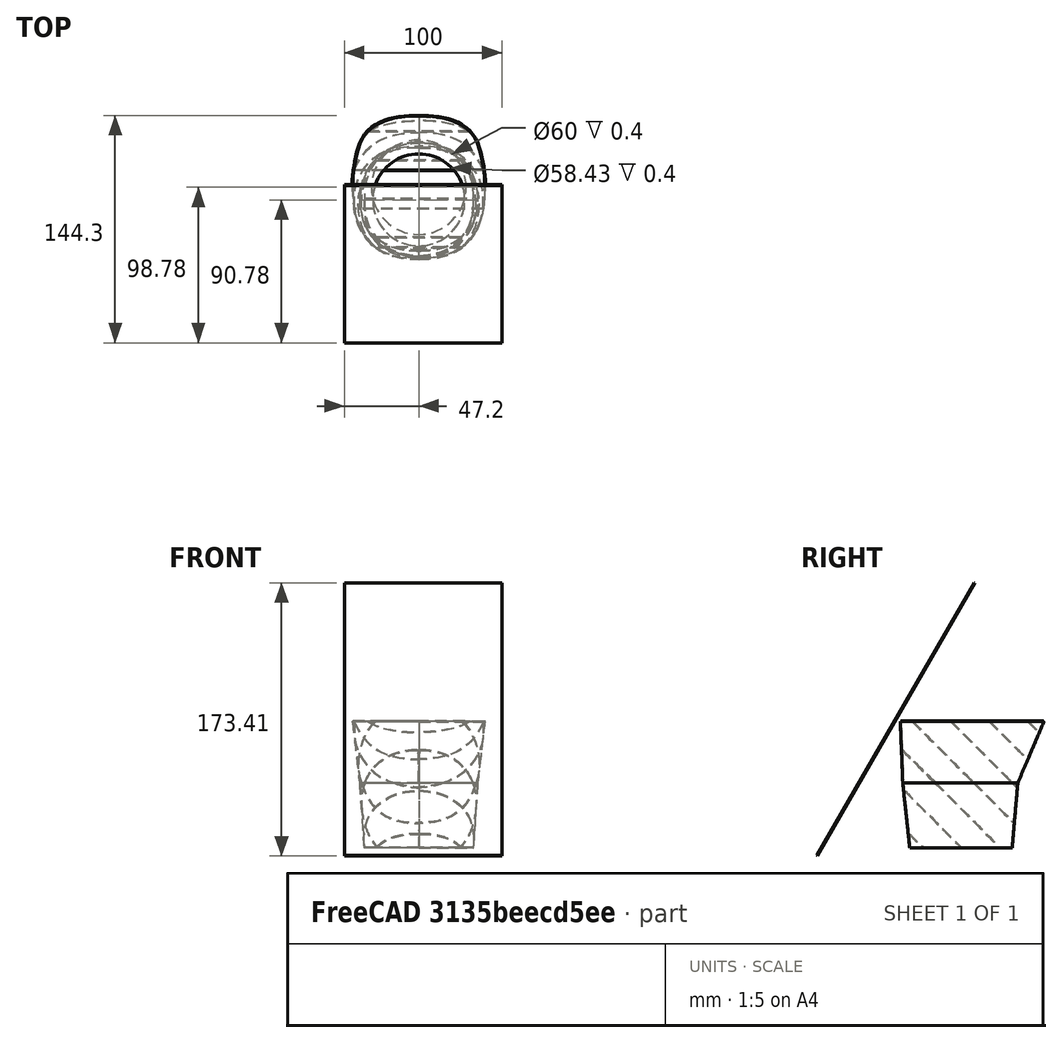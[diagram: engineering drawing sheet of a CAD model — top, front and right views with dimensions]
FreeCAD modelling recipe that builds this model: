
FCSTD DOCUMENT  (FreeCAD 0.21R33694 (Git))
Label: nose
License: All rights reserved
LicenseURL: http://en.wikipedia.org/wiki/All_rights_reserved
objects: Sketcher::SketchObject×14, PartDesign::Body×7, PartDesign::AdditiveLoft×6, Image::ImagePlane×4, Part::MultiFuse×3, PartDesign::Thickness×2, Part::Box×2, Part::MultiCommon×2, App::MeasureDistance×1, Part::FeaturePython×1, Part::Cylinder×1, Part::Cut×1, PartDesign::Pad×1, PartDesign::Pocket×1
note: 50 computed .brp shape members not serialized (recipe doc carries the construction recipe); baked Part::Feature solids carry a one-line shape summary decoded from their .brp

FEATURE [Image::ImagePlane] Screenshot_from_2023_10_14_23_56_05  label="Screenshot from 2023-10-14 23-56-05"
  Placement = pos=(-1.3,0,0) rot=(0,0,1;0rad)
  XSize = 117.558
  YSize = 96.0835
FEATURE [Image::ImagePlane] Screenshot_from_2023_10_14_23_55_51  label="Screenshot from 2023-10-14 23-55-51"
  Placement = pos=(-6,0.8,0) rot=(0,0,1;0rad)
  XSize = 153.658
  YSize = 119.36
FEATURE [Image::ImagePlane] Screenshot_from_2023_10_14_23_56_29  label="Screenshot from 2023-10-14 23-56-29"
  Placement = pos=(-8.1,5.1,0) rot=(0,0,1;0rad)
  XSize = 174.967
  YSize = 118.829
FEATURE [Sketcher::SketchObject] Sketch
  FullyConstrained = false
  MapMode = 5
  Support = -> [XY_Plane]
  sketch-geometry (10):
    g0-g4: Circle x5 (B-spline internal-alignment scaffolding for g5; pole/knot coordinates omitted)
    g5: BSplineCurve PolesCount=5 KnotsCount=3 Degree=3 IsPeriodic=0
    g6: GeomPoint X=0 Y=32.9051 Z=0
    g7: GeomPoint X=34.5313 Y=0.497786 Z=0
    g8: GeomPoint X=0 Y=-31.3846 Z=0
    g9: BSplineCurve PolesCount=5 KnotsCount=3 Degree=3 IsPeriodic=0
  constraints (12):
    c: Weight(g0) = 1
    c: PointOnObject(g5,g-2)
    c: Equal(g0,g1)
    c: Equal(g0,g2)
    c: PointOnObject(g2,g-1)
    c: Equal(g0,g3)
    c: Equal(g0,g4)
    c: PointOnObject(g5,g-2)
    c: InternalAlignment(g0-g4 -> g5) x5
    c: InternalAlignment(g6,g5)
    c: InternalAlignment(g7,g5)
    c: InternalAlignment(g8,g5)
FEATURE [Sketcher::SketchObject] Sketch001
  AttachmentOffset = pos=(0,0,41) rot=(0,0,1;0rad)
  FullyConstrained = false
  MapMode = 5
  Placement = pos=(0,0,41) rot=(0,0,1;0rad)
  Support = -> [XY_Plane]
  sketch-geometry (10):
    g0-g4: Circle x5 (B-spline internal-alignment scaffolding for g5; pole/knot coordinates omitted)
    g5: BSplineCurve PolesCount=5 KnotsCount=3 Degree=3 IsPeriodic=0
    g6: GeomPoint X=0 Y=36.497 Z=0
    g7: GeomPoint X=37.3042 Y=0.119484 Z=0
    g8: GeomPoint X=0 Y=-35.8137 Z=0
    g9: BSplineCurve PolesCount=5 KnotsCount=3 Degree=3 IsPeriodic=0
  constraints (12):
    c: Weight(g0) = 1
    c: PointOnObject(g5,g-2)
    c: Equal(g0,g1)
    c: Equal(g0,g2)
    c: PointOnObject(g2,g-1)
    c: Equal(g0,g3)
    c: Equal(g0,g4)
    c: PointOnObject(g5,g-2)
    c: InternalAlignment(g0-g4 -> g5) x5
    c: InternalAlignment(g6,g5)
    c: InternalAlignment(g7,g5)
    c: InternalAlignment(g8,g5)
FEATURE [Sketcher::SketchObject] Sketch004
  AttachmentOffset = pos=(0,0,41) rot=(0,0,1;0rad)
  FullyConstrained = false
  MapMode = 5
  Placement = pos=(0,0,41) rot=(0,0,1;0rad)
  Support = -> [XY_Plane001]
  sketch-geometry (10):
    g0-g4: Circle x5 (B-spline internal-alignment scaffolding for g5; pole/knot coordinates omitted)
    g5: BSplineCurve PolesCount=5 KnotsCount=3 Degree=3 IsPeriodic=0
    g6: GeomPoint X=0 Y=36.497 Z=0
    g7: GeomPoint X=37.3042 Y=0.119484 Z=0
    g8: GeomPoint X=0 Y=-35.8137 Z=0
    g9: BSplineCurve PolesCount=5 KnotsCount=3 Degree=3 IsPeriodic=0
  constraints (12):
    c: Weight(g0) = 1
    c: PointOnObject(g5,g-2)
    c: Equal(g0,g1)
    c: Equal(g0,g2)
    c: PointOnObject(g2,g-1)
    c: Equal(g0,g3)
    c: Equal(g0,g4)
    c: PointOnObject(g5,g-2)
    c: InternalAlignment(g0-g4 -> g5) x5
    c: InternalAlignment(g6,g5)
    c: InternalAlignment(g7,g5)
    c: InternalAlignment(g8,g5)
FEATURE [Sketcher::SketchObject] Sketch005
  AttachmentOffset = pos=(0,0,80) rot=(0,0,1;0rad)
  FullyConstrained = false
  MapMode = 5
  Placement = pos=(0,0,80) rot=(0,0,1;0rad)
  Support = -> [XY_Plane001]
  sketch-geometry (16):
    g0-g7: Circle x8 (B-spline internal-alignment scaffolding for g8; pole/knot coordinates omitted)
    g8: BSplineCurve PolesCount=8 KnotsCount=6 Degree=3 IsPeriodic=0
    g9-g14: GeomPoint x6 (B-spline internal-alignment scaffolding for g8; pole/knot coordinates omitted)
    g15: BSplineCurve PolesCount=8 KnotsCount=6 Degree=3 IsPeriodic=0
  constraints (10):
    c: Weight(g0) = 1
    c: PointOnObject(g8,g-2)
    c: Equal(g0, g1-g4) x4
    c: PointOnObject(g4,g-1)
    c: Equal(g0,g5)
    c: Equal(g0,g6)
    c: Equal(g0,g7)
    c: PointOnObject(g8,g-2)
    c: InternalAlignment(g0-g7 -> g8) x8
    c: InternalAlignment(g9-g14 -> g8) x6
FEATURE [PartDesign::AdditiveLoft] AdditiveLoft
  Closed = false
  Profile = -> Sketch001
  Ruled = true
  Sections = -> [Sketch]
FEATURE [PartDesign::AdditiveLoft] AdditiveLoft001
  Closed = false
  Profile = -> Sketch005
  Ruled = true
  Sections = -> [Sketch004]
FEATURE [App::MeasureDistance] Distance  label="Distance: 64.29 mm"
  Distance = 64.2866
  P1 = (-0.105968,32.9036,0)
  P2 = (-0.0834491,-31.3831,0)
FEATURE [Image::ImagePlane] Screenshot_from_2023_10_15_16_07_44  label="Screenshot from 2023-10-15 16-07-44"
  Placement = pos=(-1e-14,17.7,44.9) rot=(0,1,0;4.71239rad)
  XSize = 263.435
  YSize = 168.665
FEATURE [Sketcher::SketchObject] Sketch006
  AttachmentOffset = pos=(0,0,41) rot=(0,0,1;0rad)
  FullyConstrained = false
  MapMode = 5
  Placement = pos=(0,0,41) rot=(0,0,1;0rad)
  Support = -> [XY_Plane002]
  sketch-geometry (10):
    g0-g4: Circle x5 (B-spline internal-alignment scaffolding for g5; pole/knot coordinates omitted)
    g5: BSplineCurve PolesCount=5 KnotsCount=3 Degree=3 IsPeriodic=0
    g6: GeomPoint X=0 Y=36.497 Z=0
    g7: GeomPoint X=37.3042 Y=0.119484 Z=0
    g8: GeomPoint X=0 Y=-35.8137 Z=0
    g9: BSplineCurve PolesCount=5 KnotsCount=3 Degree=3 IsPeriodic=0
  constraints (12):
    c: Weight(g0) = 1
    c: PointOnObject(g5,g-2)
    c: Equal(g0,g1)
    c: Equal(g0,g2)
    c: PointOnObject(g2,g-1)
    c: Equal(g0,g3)
    c: Equal(g0,g4)
    c: PointOnObject(g5,g-2)
    c: InternalAlignment(g0-g4 -> g5) x5
    c: InternalAlignment(g6,g5)
    c: InternalAlignment(g7,g5)
    c: InternalAlignment(g8,g5)
FEATURE [Sketcher::SketchObject] Sketch007
  AttachmentOffset = pos=(0,0,80) rot=(0,0,1;0rad)
  FullyConstrained = false
  MapMode = 5
  Placement = pos=(0,0,80) rot=(0,0,1;0rad)
  Support = -> [XY_Plane002]
  sketch-geometry (16):
    g0-g7: Circle x8 (B-spline internal-alignment scaffolding for g8; pole/knot coordinates omitted)
    g8: BSplineCurve PolesCount=8 KnotsCount=6 Degree=3 IsPeriodic=0
    g9-g14: GeomPoint x6 (B-spline internal-alignment scaffolding for g8; pole/knot coordinates omitted)
    g15: BSplineCurve PolesCount=8 KnotsCount=6 Degree=3 IsPeriodic=0
  constraints (10):
    c: Weight(g0) = 1
    c: PointOnObject(g8,g-2)
    c: Equal(g0, g1-g4) x4
    c: PointOnObject(g4,g-1)
    c: Equal(g0,g5)
    c: Equal(g0,g6)
    c: Equal(g0,g7)
    c: PointOnObject(g8,g-2)
    c: InternalAlignment(g0-g7 -> g8) x8
    c: InternalAlignment(g9-g14 -> g8) x6
FEATURE [PartDesign::AdditiveLoft] AdditiveLoft002
  Closed = false
  Profile = -> Sketch007
  Ruled = true
  Sections = -> [Sketch006]
FEATURE [PartDesign::Body] Body002
  Group = -> [Sketch006,Sketch007,AdditiveLoft002]
  Origin = -> Origin002
  Tip = -> AdditiveLoft002
FEATURE [Sketcher::SketchObject] Sketch008
  FullyConstrained = false
  MapMode = 5
  Support = -> [XY_Plane003]
  sketch-geometry (10):
    g0-g4: Circle x5 (B-spline internal-alignment scaffolding for g5; pole/knot coordinates omitted)
    g5: BSplineCurve PolesCount=5 KnotsCount=3 Degree=3 IsPeriodic=0
    g6: GeomPoint X=0 Y=32.9051 Z=0
    g7: GeomPoint X=34.5313 Y=0.497786 Z=0
    g8: GeomPoint X=0 Y=-31.3846 Z=0
    g9: BSplineCurve PolesCount=5 KnotsCount=3 Degree=3 IsPeriodic=0
  constraints (12):
    c: Weight(g0) = 1
    c: PointOnObject(g5,g-2)
    c: Equal(g0,g1)
    c: Equal(g0,g2)
    c: PointOnObject(g2,g-1)
    c: Equal(g0,g3)
    c: Equal(g0,g4)
    c: PointOnObject(g5,g-2)
    c: InternalAlignment(g0-g4 -> g5) x5
    c: InternalAlignment(g6,g5)
    c: InternalAlignment(g7,g5)
    c: InternalAlignment(g8,g5)
FEATURE [Sketcher::SketchObject] Sketch009
  AttachmentOffset = pos=(0,0,41) rot=(0,0,1;0rad)
  FullyConstrained = false
  MapMode = 5
  Placement = pos=(0,0,41) rot=(0,0,1;0rad)
  Support = -> [XY_Plane003]
  sketch-geometry (10):
    g0-g4: Circle x5 (B-spline internal-alignment scaffolding for g5; pole/knot coordinates omitted)
    g5: BSplineCurve PolesCount=5 KnotsCount=3 Degree=3 IsPeriodic=0
    g6: GeomPoint X=0 Y=36.497 Z=0
    g7: GeomPoint X=37.3042 Y=0.119484 Z=0
    g8: GeomPoint X=0 Y=-35.8137 Z=0
    g9: BSplineCurve PolesCount=5 KnotsCount=3 Degree=3 IsPeriodic=0
  constraints (12):
    c: Weight(g0) = 1
    c: PointOnObject(g5,g-2)
    c: Equal(g0,g1)
    c: Equal(g0,g2)
    c: PointOnObject(g2,g-1)
    c: Equal(g0,g3)
    c: Equal(g0,g4)
    c: PointOnObject(g5,g-2)
    c: InternalAlignment(g0-g4 -> g5) x5
    c: InternalAlignment(g6,g5)
    c: InternalAlignment(g7,g5)
    c: InternalAlignment(g8,g5)
FEATURE [PartDesign::AdditiveLoft] AdditiveLoft003
  Closed = false
  Profile = -> Sketch009
  Ruled = true
  Sections = -> [Sketch008]
FEATURE [PartDesign::Body] Body003
  Group = -> [Sketch008,Sketch009,AdditiveLoft003]
  Origin = -> Origin003
  Tip = -> AdditiveLoft003
FEATURE [PartDesign::Thickness] Thickness
  Base = -> AdditiveLoft [Face1]
  BaseFeature = -> AdditiveLoft
  Intersection = false
  Join = 1
  Mode = 0
  SupportTransform = false
  Value = 0.4
FEATURE [PartDesign::Body] Body
  Group = -> [Sketch,Sketch001,AdditiveLoft,Thickness]
  Origin = -> Origin
  Tip = -> Thickness
FEATURE [PartDesign::Thickness] Thickness001
  Base = -> AdditiveLoft001 [Face1,Face3]
  BaseFeature = -> AdditiveLoft001
  Intersection = false
  Join = 1
  Mode = 1
  SupportTransform = false
  Value = 0.4
FEATURE [PartDesign::Body] Body001
  Group = -> [Sketch004,Sketch005,AdditiveLoft001,Thickness001]
  Origin = -> Origin001
  Tip = -> Thickness001
FEATURE [Part::MultiFuse] Fusion001
  Shapes = -> [Body002,Body003]
FEATURE [Part::Box] Box  label="Cube"
  AttacherType = Attacher::AttachEngine3D
  Height = 200
  Length = 100
  Placement = pos=(-47.2,-90.7758,-5.26929) rot=(-1,0,0;0.523599rad)
  Width = 0.4
FEATURE [Part::FeaturePython] Array  # Draft array (typed FeaturePython)
  AlwaysSyncPlacement = false
  Angle = 360
  ArrayType = 0
  Axis = (0,0,1)
  Base = -> Box
  Center = (0,0,0)
  Count = 9
  ExpandArray = false
  Fuse = false
  IntervalAxis = (0,0,0)
  IntervalX = (100,0,0)
  IntervalY = (0,20,0)
  IntervalZ = (0,0,20)
  NumberCircles = 3
  NumberPolar = 5
  NumberX = 1
  NumberY = 9
  NumberZ = 1
  Placement = pos=(0,84.5954,-1.10956) rot=(1,0,0;1.309rad)
  PlacementList = 9 placements: arithmetic series from (-47.2,-90.7758,-5.26929) step (0,20,0) to (-47.2,69.2242,-5.26929)
  RadialDistance = 50
  ScaleList = (9) [(1,1,1),(1,1,1),(1,1,1),(1,1,1),(1,1,1),(1,1,1),(1,1,1),(1,1,1),(1,1,1)]
  Symmetry = 1
  TangentialDistance = 25
FEATURE [Part::MultiCommon] Common
  Shapes = -> [Fusion001,Array]
FEATURE [Sketcher::SketchObject] Sketch010
  AttachmentOffset = pos=(0,0,41) rot=(0,0,1;0rad)
  FullyConstrained = false
  MapMode = 5
  Placement = pos=(0,0,41) rot=(0,0,1;0rad)
  Support = -> [XY_Plane004]
  sketch-geometry (10):
    g0-g4: Circle x5 (B-spline internal-alignment scaffolding for g5; pole/knot coordinates omitted)
    g5: BSplineCurve PolesCount=5 KnotsCount=3 Degree=3 IsPeriodic=0
    g6: GeomPoint X=0 Y=36.497 Z=0
    g7: GeomPoint X=37.3042 Y=0.119484 Z=0
    g8: GeomPoint X=0 Y=-35.8137 Z=0
    g9: BSplineCurve PolesCount=5 KnotsCount=3 Degree=3 IsPeriodic=0
  constraints (12):
    c: Weight(g0) = 1
    c: PointOnObject(g5,g-2)
    c: Equal(g0,g1)
    c: Equal(g0,g2)
    c: PointOnObject(g2,g-1)
    c: Equal(g0,g3)
    c: Equal(g0,g4)
    c: PointOnObject(g5,g-2)
    c: InternalAlignment(g0-g4 -> g5) x5
    c: InternalAlignment(g6,g5)
    c: InternalAlignment(g7,g5)
    c: InternalAlignment(g8,g5)
FEATURE [Sketcher::SketchObject] Sketch011
  AttachmentOffset = pos=(0,0,80) rot=(0,0,1;0rad)
  FullyConstrained = false
  MapMode = 5
  Placement = pos=(0,0,80) rot=(0,0,1;0rad)
  Support = -> [XY_Plane004]
  sketch-geometry (16):
    g0-g7: Circle x8 (B-spline internal-alignment scaffolding for g8; pole/knot coordinates omitted)
    g8: BSplineCurve PolesCount=8 KnotsCount=6 Degree=3 IsPeriodic=0
    g9-g14: GeomPoint x6 (B-spline internal-alignment scaffolding for g8; pole/knot coordinates omitted)
    g15: BSplineCurve PolesCount=8 KnotsCount=6 Degree=3 IsPeriodic=0
  constraints (10):
    c: Weight(g0) = 1
    c: PointOnObject(g8,g-2)
    c: Equal(g0, g1-g4) x4
    c: PointOnObject(g4,g-1)
    c: Equal(g0,g5)
    c: Equal(g0,g6)
    c: Equal(g0,g7)
    c: PointOnObject(g8,g-2)
    c: InternalAlignment(g0-g7 -> g8) x8
    c: InternalAlignment(g9-g14 -> g8) x6
FEATURE [PartDesign::AdditiveLoft] AdditiveLoft004
  Closed = false
  Profile = -> Sketch011
  Ruled = true
  Sections = -> [Sketch010]
FEATURE [PartDesign::Body] Body004
  Group = -> [Sketch010,Sketch011,AdditiveLoft004]
  Origin = -> Origin004
  Tip = -> AdditiveLoft004
FEATURE [Sketcher::SketchObject] Sketch012
  FullyConstrained = false
  MapMode = 5
  Support = -> [XY_Plane005]
  sketch-geometry (10):
    g0-g4: Circle x5 (B-spline internal-alignment scaffolding for g5; pole/knot coordinates omitted)
    g5: BSplineCurve PolesCount=5 KnotsCount=3 Degree=3 IsPeriodic=0
    g6: GeomPoint X=0 Y=32.9051 Z=0
    g7: GeomPoint X=34.5313 Y=0.497786 Z=0
    g8: GeomPoint X=0 Y=-31.3846 Z=0
    g9: BSplineCurve PolesCount=5 KnotsCount=3 Degree=3 IsPeriodic=0
  constraints (12):
    c: Weight(g0) = 1
    c: PointOnObject(g5,g-2)
    c: Equal(g0,g1)
    c: Equal(g0,g2)
    c: PointOnObject(g2,g-1)
    c: Equal(g0,g3)
    c: Equal(g0,g4)
    c: PointOnObject(g5,g-2)
    c: InternalAlignment(g0-g4 -> g5) x5
    c: InternalAlignment(g6,g5)
    c: InternalAlignment(g7,g5)
    c: InternalAlignment(g8,g5)
FEATURE [Sketcher::SketchObject] Sketch013
  AttachmentOffset = pos=(0,0,41) rot=(0,0,1;0rad)
  FullyConstrained = false
  MapMode = 5
  Placement = pos=(0,0,41) rot=(0,0,1;0rad)
  Support = -> [XY_Plane005]
  sketch-geometry (10):
    g0-g4: Circle x5 (B-spline internal-alignment scaffolding for g5; pole/knot coordinates omitted)
    g5: BSplineCurve PolesCount=5 KnotsCount=3 Degree=3 IsPeriodic=0
    g6: GeomPoint X=0 Y=36.497 Z=0
    g7: GeomPoint X=37.3042 Y=0.119484 Z=0
    g8: GeomPoint X=0 Y=-35.8137 Z=0
    g9: BSplineCurve PolesCount=5 KnotsCount=3 Degree=3 IsPeriodic=0
  constraints (12):
    c: Weight(g0) = 1
    c: PointOnObject(g5,g-2)
    c: Equal(g0,g1)
    c: Equal(g0,g2)
    c: PointOnObject(g2,g-1)
    c: Equal(g0,g3)
    c: Equal(g0,g4)
    c: PointOnObject(g5,g-2)
    c: InternalAlignment(g0-g4 -> g5) x5
    c: InternalAlignment(g6,g5)
    c: InternalAlignment(g7,g5)
    c: InternalAlignment(g8,g5)
FEATURE [PartDesign::AdditiveLoft] AdditiveLoft005
  Closed = false
  Profile = -> Sketch013
  Ruled = true
  Sections = -> [Sketch012]
FEATURE [PartDesign::Body] Body005
  Group = -> [Sketch012,Sketch013,AdditiveLoft005]
  Origin = -> Origin005
  Tip = -> AdditiveLoft005
FEATURE [Part::MultiFuse] Fusion
  Shapes = -> [Common,Body,Body001]
FEATURE [Part::MultiFuse] Fusion003
  Shapes = -> [Body004,Body005]
FEATURE [Part::Box] Box001  label="Cube001"
  AttacherType = Attacher::AttachEngine3D
  Height = 0.4
  Length = 100
  Placement = pos=(-53,-45.8,79.6) rot=(0,0,1;0rad)
  Width = 100
FEATURE [Part::Cylinder] Cylinder
  Angle = 360
  AttacherType = Attacher::AttachEngine3D
  FirstAngle = 0
  Height = 10
  Placement = pos=(0,8,78.2) rot=(0,0,1;0rad)
  Radius = 30
  SecondAngle = 0
FEATURE [Part::MultiCommon] Common001
  Shapes = -> [Fusion003,Box001]
FEATURE [Part::Cut] Cut
  Base = -> Common001
  Tool = -> Cylinder
FEATURE [Sketcher::SketchObject] Sketch014
  AttachmentOffset = pos=(0,0,80) rot=(0,0,1;0rad)
  FullyConstrained = false
  MapMode = 5
  Placement = pos=(0,0,80) rot=(0,0,1;0rad)
  Support = -> [XY_Plane006]
  sketch-geometry (16):
    g0-g7: Circle x8 (B-spline internal-alignment scaffolding for g8; pole/knot coordinates omitted)
    g8: BSplineCurve PolesCount=8 KnotsCount=6 Degree=3 IsPeriodic=0
    g9-g14: GeomPoint x6 (B-spline internal-alignment scaffolding for g8; pole/knot coordinates omitted)
    g15: BSplineCurve PolesCount=8 KnotsCount=6 Degree=3 IsPeriodic=0
  constraints (10):
    c: Weight(g0) = 1
    c: PointOnObject(g8,g-2)
    c: Equal(g0, g1-g4) x4
    c: PointOnObject(g4,g-1)
    c: Equal(g0,g5)
    c: Equal(g0,g6)
    c: Equal(g0,g7)
    c: PointOnObject(g8,g-2)
    c: InternalAlignment(g0-g7 -> g8) x8
    c: InternalAlignment(g9-g14 -> g8) x6
FEATURE [PartDesign::Pad] Pad
  Direction = (0,0,1)
  Length = 0.4
  Length2 = 10
  Profile = -> Sketch014
  ReferenceAxis = -> Sketch014 [N_Axis]
  Type = 0
FEATURE [Sketcher::SketchObject] Sketch015
  FullyConstrained = false
  MapMode = 5
  Placement = pos=(0,0,80.4) rot=(0,0,1;0rad)
  Support = -> [Pad]
  sketch-geometry (1):
    g0: Circle CenterX=0 CenterY=0 CenterZ=0 NormalX=0 NormalY=0 NormalZ=1 AngleXU=0 Radius=29.2164
  constraints (1):
    c: Coincident(g0,g-1)
FEATURE [PartDesign::Pocket] Pocket
  BaseFeature = -> Pad
  Direction = (0,0,-1)
  Length = 5
  Length2 = 5
  Profile = -> Sketch015
  ReferenceAxis = -> Sketch015 [N_Axis]
  Type = 0
FEATURE [PartDesign::Body] Body006
  Group = -> [Sketch014,Pad,Sketch015,Pocket]
  Origin = -> Origin006
  Tip = -> Pocket
